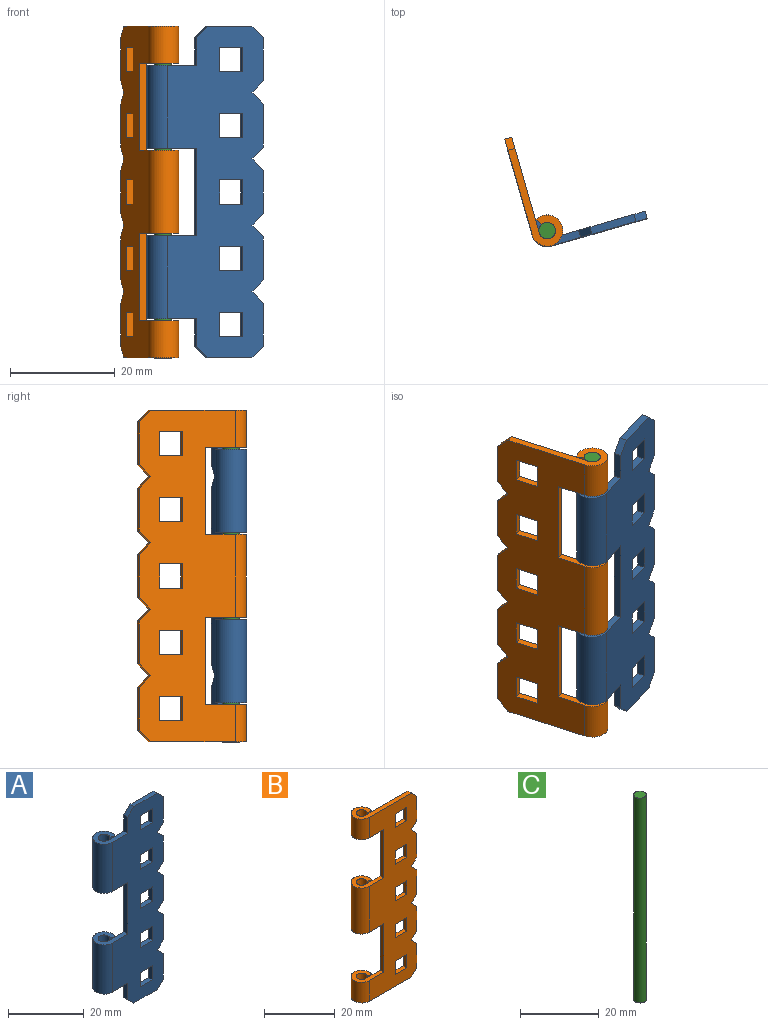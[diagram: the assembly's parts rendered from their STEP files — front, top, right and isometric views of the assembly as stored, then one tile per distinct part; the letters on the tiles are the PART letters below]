
ASSEMBLY  parts=3 mates=3
PART A: 54 faces, bbox 22.1x6x63.5 mm
  f0: cylinder r=3.01mm len=15.88mm, axis (0,0,1), area 250.2mm2, adj f5,f43,f44,f48
  f1: cylinder r=1.59mm len=15.88mm, axis (0,0,1), area 132mm2, adj f4,f43,f44,f48
  f2: cylinder r=3.01mm len=15.88mm, axis (0,0,1), area 250.2mm2, adj f5,f45,f46,f47
  f3: cylinder r=1.59mm len=15.88mm, axis (0,0,1), area 132mm2, adj f4,f45,f46,f47
  f4: plane 63.5x19.05mm, normal (0,1,0), area 888.2mm2, adj f1,f3,f6,f7,f8,f9,f10,f11
  f5: plane 63.5x19.05mm, normal (0,-1,0), area 888.2mm2, adj f0,f2,f6,f7,f8,f9,f10,f11
  f6: plane 16.69x1.42mm, normal (-1,0,0), area 23.7mm2, adj f4,f5,f44,f45
  f7: plane 5.29x1.42mm, normal (-1,0,0), area 7.5mm2, adj f4,f5,f8,f46
  f8: plane 2.25x2.25mm, normal (-0.71,0,-0.71), area 4.5mm2, adj f4,f5,f7,f9
  f9: plane 8.75x1.42mm, normal (0,0,-1), area 12.4mm2, adj f4,f5,f8,f10
  f10: plane 2.25x2.25mm, normal (0.71,0,-0.71), area 4.5mm2, adj f4,f5,f9,f50
  f11: plane 2.25x2.25mm, normal (0.71,0,0.71), area 4.5mm2, adj f4,f5,f12,f49
  f12: plane 8.75x1.42mm, normal (0,0,1), area 12.4mm2, adj f4,f5,f11,f13
  f13: plane 2.25x2.25mm, normal (-0.71,0,0.71), area 4.5mm2, adj f4,f5,f12,f14
  f14: plane 5.29x1.42mm, normal (-1,0,0), area 7.5mm2, adj f4,f5,f13,f43
  f15: plane 4.62x1.42mm, normal (1,0,0), area 6.6mm2, adj f4,f5,f16,f18
  f16: plane 4.62x1.42mm, normal (0,0,-1), area 6.6mm2, adj f4,f5,f15,f17
  f17: plane 4.62x1.42mm, normal (-1,0,0), area 6.6mm2, adj f4,f5,f16,f18
  f18: plane 4.62x1.42mm, normal (0,0,1), area 6.6mm2, adj f4,f5,f15,f17
  f19: plane 4.62x1.42mm, normal (1,0,0), area 6.6mm2, adj f4,f5,f20,f22
  f20: plane 4.62x1.42mm, normal (0,0,-1), area 6.6mm2, adj f4,f5,f19,f21
  f21: plane 4.62x1.42mm, normal (-1,0,0), area 6.6mm2, adj f4,f5,f20,f22
  f22: plane 4.62x1.42mm, normal (0,0,1), area 6.6mm2, adj f4,f5,f19,f21
  f23: plane 4.62x1.42mm, normal (1,0,0), area 6.6mm2, adj f4,f5,f24,f26
  f24: plane 4.62x1.42mm, normal (0,0,-1), area 6.6mm2, adj f4,f5,f23,f25
  f25: plane 4.62x1.42mm, normal (-1,0,0), area 6.6mm2, adj f4,f5,f24,f26
  f26: plane 4.62x1.42mm, normal (0,0,1), area 6.6mm2, adj f4,f5,f23,f25
  f27: plane 4.62x1.42mm, normal (1,0,0), area 6.6mm2, adj f4,f5,f28,f30
  f28: plane 4.62x1.42mm, normal (0,0,-1), area 6.6mm2, adj f4,f5,f27,f29
  f29: plane 4.62x1.42mm, normal (-1,0,0), area 6.6mm2, adj f4,f5,f28,f30
  f30: plane 4.62x1.42mm, normal (0,0,1), area 6.6mm2, adj f4,f5,f27,f29
  f31: plane 4.62x1.42mm, normal (1,0,0), area 6.6mm2, adj f4,f5,f32,f34
  f32: plane 4.62x1.42mm, normal (0,0,-1), area 6.6mm2, adj f4,f5,f31,f33
  f33: plane 4.62x1.42mm, normal (-1,0,0), area 6.6mm2, adj f4,f5,f32,f34
  f34: plane 4.62x1.42mm, normal (0,0,1), area 6.6mm2, adj f4,f5,f31,f33
  f35: plane 2.25x2.25mm, normal (0.71,0,0.71), area 4.5mm2, adj f4,f5,f36,f53
  f36: plane 2.25x2.25mm, normal (0.71,0,-0.71), area 4.5mm2, adj f4,f5,f35,f49
  f37: plane 2.25x2.25mm, normal (0.71,0,0.71), area 4.5mm2, adj f4,f5,f38,f52
  f38: plane 2.25x2.25mm, normal (0.71,0,-0.71), area 4.5mm2, adj f4,f5,f37,f53
  f39: plane 2.25x2.25mm, normal (0.71,0,0.71), area 4.5mm2, adj f4,f5,f40,f51
  f40: plane 2.25x2.25mm, normal (0.71,0,-0.71), area 4.5mm2, adj f4,f5,f39,f52
  f41: plane 2.25x2.25mm, normal (0.71,0,0.71), area 4.5mm2, adj f4,f5,f42,f50
  f42: plane 2.25x2.25mm, normal (0.71,0,-0.71), area 4.5mm2, adj f4,f5,f41,f51
  f43: plane 8.82x6.02mm, normal (0,0,1), area 25.4mm2, adj f0,f1,f4,f5,f14,f48
  f44: plane 8.82x6.02mm, normal (0,0,-1), area 25.4mm2, adj f0,f1,f4,f5,f6,f48
  f45: plane 8.82x6.02mm, normal (0,0,1), area 25.4mm2, adj f2,f3,f4,f5,f6,f47
  f46: plane 8.82x6.02mm, normal (0,0,-1), area 25.4mm2, adj f2,f3,f4,f5,f7,f47
  f47: plane 15.88x1.23mm, normal (-0.5,-0.87,0), area 22.6mm2, adj f2,f3,f45,f46
  f48: plane 15.88x1.23mm, normal (-0.5,-0.87,0), area 22.6mm2, adj f0,f1,f43,f44
  f49: plane 8.21x1.42mm, normal (1,0,0), area 11.7mm2, adj f4,f5,f11,f36
  f50: plane 8.21x1.42mm, normal (1,0,0), area 11.7mm2, adj f4,f5,f10,f41
  f51: plane 8.21x1.42mm, normal (1,0,0), area 11.7mm2, adj f4,f5,f39,f42
  f52: plane 8.21x1.42mm, normal (1,0,0), area 11.7mm2, adj f4,f5,f37,f40
  f53: plane 8.21x1.42mm, normal (1,0,0), area 11.7mm2, adj f4,f5,f35,f38
PART B: 54 faces, bbox 22x6x63.5 mm
  f0: cylinder r=2.98mm len=7.12mm, axis (0,0,1), area 111.3mm2, adj f7,f40,f41,f48
  f1: cylinder r=1.59mm len=7.12mm, axis (0,0,1), area 59.2mm2, adj f6,f40,f41,f48
  f2: cylinder r=2.98mm len=15.88mm, axis (0,0,1), area 248.1mm2, adj f7,f44,f45,f47
  f3: cylinder r=1.59mm len=15.88mm, axis (0,0,1), area 132mm2, adj f6,f44,f45,f47
  f4: cylinder r=2.98mm len=7.12mm, axis (0,0,1), area 111.3mm2, adj f7,f42,f43,f46
  f5: cylinder r=1.59mm len=7.12mm, axis (0,0,1), area 59.2mm2, adj f6,f42,f43,f46
  f6: plane 63.5x19.05mm, normal (0,1,0), area 882.3mm2, adj f1,f3,f5,f8,f9,f10,f11,f12
  f7: plane 63.5x19.05mm, normal (0,-1,0), area 882.3mm2, adj f0,f2,f4,f8,f9,f10,f11,f12
  f8: plane 2.25x2.25mm, normal (0.71,0,0.71), area 4.4mm2, adj f6,f7,f40,f49
  f9: plane 16.69x1.4mm, normal (-1,0,0), area 23.3mm2, adj f6,f7,f41,f44
  f10: plane 16.69x1.4mm, normal (-1,0,0), area 23.3mm2, adj f6,f7,f42,f45
  f11: plane 2.25x2.25mm, normal (0.71,0,-0.71), area 4.4mm2, adj f6,f7,f43,f50
  f12: plane 4.62x1.4mm, normal (1,0,0), area 6.5mm2, adj f6,f7,f13,f15
  f13: plane 4.62x1.4mm, normal (0,0,-1), area 6.5mm2, adj f6,f7,f12,f14
  f14: plane 4.62x1.4mm, normal (-1,0,0), area 6.5mm2, adj f6,f7,f13,f15
  f15: plane 4.62x1.4mm, normal (0,0,1), area 6.5mm2, adj f6,f7,f12,f14
  f16: plane 4.62x1.4mm, normal (1,0,0), area 6.5mm2, adj f6,f7,f17,f19
  f17: plane 4.62x1.4mm, normal (0,0,-1), area 6.5mm2, adj f6,f7,f16,f18
  f18: plane 4.62x1.4mm, normal (-1,0,0), area 6.5mm2, adj f6,f7,f17,f19
  f19: plane 4.62x1.4mm, normal (0,0,1), area 6.5mm2, adj f6,f7,f16,f18
  f20: plane 4.62x1.4mm, normal (1,0,0), area 6.5mm2, adj f6,f7,f21,f23
  f21: plane 4.62x1.4mm, normal (0,0,-1), area 6.5mm2, adj f6,f7,f20,f22
  f22: plane 4.62x1.4mm, normal (-1,0,0), area 6.5mm2, adj f6,f7,f21,f23
  f23: plane 4.62x1.4mm, normal (0,0,1), area 6.5mm2, adj f6,f7,f20,f22
  f24: plane 4.62x1.4mm, normal (1,0,0), area 6.5mm2, adj f6,f7,f25,f27
  f25: plane 4.62x1.4mm, normal (0,0,-1), area 6.5mm2, adj f6,f7,f24,f26
  f26: plane 4.62x1.4mm, normal (-1,0,0), area 6.5mm2, adj f6,f7,f25,f27
  f27: plane 4.62x1.4mm, normal (0,0,1), area 6.5mm2, adj f6,f7,f24,f26
  f28: plane 4.62x1.4mm, normal (1,0,0), area 6.5mm2, adj f6,f7,f29,f31
  f29: plane 4.62x1.4mm, normal (0,0,-1), area 6.5mm2, adj f6,f7,f28,f30
  f30: plane 4.62x1.4mm, normal (-1,0,0), area 6.5mm2, adj f6,f7,f29,f31
  f31: plane 4.62x1.4mm, normal (0,0,1), area 6.5mm2, adj f6,f7,f28,f30
  f32: plane 2.25x2.25mm, normal (0.71,0,0.71), area 4.4mm2, adj f6,f7,f33,f53
  f33: plane 2.25x2.25mm, normal (0.71,0,-0.71), area 4.4mm2, adj f6,f7,f32,f49
  f34: plane 2.25x2.25mm, normal (0.71,0,0.71), area 4.4mm2, adj f6,f7,f35,f52
  f35: plane 2.25x2.25mm, normal (0.71,0,-0.71), area 4.4mm2, adj f6,f7,f34,f53
  f36: plane 2.25x2.25mm, normal (0.71,0,0.71), area 4.4mm2, adj f6,f7,f37,f51
  f37: plane 2.25x2.25mm, normal (0.71,0,-0.71), area 4.4mm2, adj f6,f7,f36,f52
  f38: plane 2.25x2.25mm, normal (0.71,0,0.71), area 4.4mm2, adj f6,f7,f39,f50
  f39: plane 2.25x2.25mm, normal (0.71,0,-0.71), area 4.4mm2, adj f6,f7,f38,f51
  f40: plane 19.79x5.97mm, normal (0,0,1), area 40.2mm2, adj f0,f1,f6,f7,f8,f48
  f41: plane 8.84x5.97mm, normal (0,0,-1), area 24.9mm2, adj f0,f1,f6,f7,f9,f48
  f42: plane 8.84x5.97mm, normal (0,0,1), area 24.9mm2, adj f4,f5,f6,f7,f10,f46
  f43: plane 19.79x5.97mm, normal (0,0,-1), area 40.2mm2, adj f4,f5,f6,f7,f11,f46
  f44: plane 8.84x5.97mm, normal (0,0,1), area 24.9mm2, adj f2,f3,f6,f7,f9,f47
  f45: plane 8.84x5.97mm, normal (0,0,-1), area 24.9mm2, adj f2,f3,f6,f7,f10,f47
  f46: plane 7.12x1.21mm, normal (-0.5,-0.87,0), area 10mm2, adj f4,f5,f42,f43
  f47: plane 15.88x1.21mm, normal (-0.5,-0.87,0), area 22.2mm2, adj f2,f3,f44,f45
  f48: plane 7.12x1.21mm, normal (-0.5,-0.87,0), area 10mm2, adj f0,f1,f40,f41
  f49: plane 8.21x1.4mm, normal (1,0,0), area 11.5mm2, adj f6,f7,f8,f33
  f50: plane 8.21x1.4mm, normal (1,0,0), area 11.5mm2, adj f6,f7,f11,f38
  f51: plane 8.21x1.4mm, normal (1,0,0), area 11.5mm2, adj f6,f7,f36,f39
  f52: plane 8.21x1.4mm, normal (1,0,0), area 11.5mm2, adj f6,f7,f34,f37
  f53: plane 8.21x1.4mm, normal (1,0,0), area 11.5mm2, adj f6,f7,f32,f35
PART C: 3 faces, bbox 3.2x3.2x63.5 mm
  f0: cylinder r=1.59mm len=63.5mm, axis (0,0,-1), area 633.4mm2, adj f1,f2
  f1: plane 3.18x3.18mm, normal (0,0,1), area 7.9mm2, adj f0
  f2: plane 3.18x3.18mm, normal (0,0,-1), area 7.9mm2, adj f0
PLACE A rot(axis=(0,0,1),16deg) t=(2.19,0.92,1.67)mm
PLACE B rot(axis=(-0.6,-0.8,0),180deg) t=(-21.15,13.87,1.67)mm
PLACE C rot(axis=(0,0,1),16deg) t=(-13.9,-0.56,-30.08)mm
MATE cylindrical A.f0 <-> C.f0  axis (0,0,1) through (-13.9,-0.56,25.89)mm
MATE planar A.f12 <-> C.f0  axis (0,0,1) through (-1.32,0.66,33.42)mm
MATE fastened C.f0 <-> B.f0  axis (0,0,1) through (-13.9,-0.56,33.42)mm
